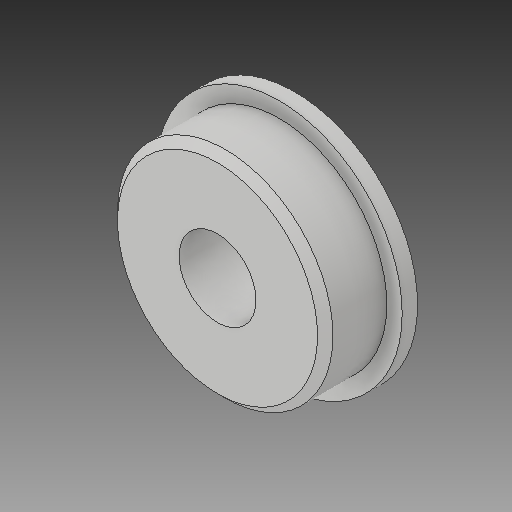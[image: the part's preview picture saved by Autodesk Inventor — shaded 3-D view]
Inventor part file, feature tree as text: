
AUTODESK INVENTOR PART (.ipt)
format: ipt  version: 2017 (Build 210142000, 142)  size: 122,880 bytes
history: native  units: mm
features: other x3, sketch x2
ambient origin geometry x8: Origin, YZ Plane, XZ Plane, XY Plane, X Axis, Y Axis, Z Axis, Center Point
bodies: Solid1 (feature_tree)
feature tree (5):
  other  "Flanged Bearing.ipt"
  other  "Solid1::Flanged Bearing.ipt"
  other  "TaggingFeature1"
  sketch  "Sketch1"  dims[d0=10.0mm]
  sketch  "Sketch2"
